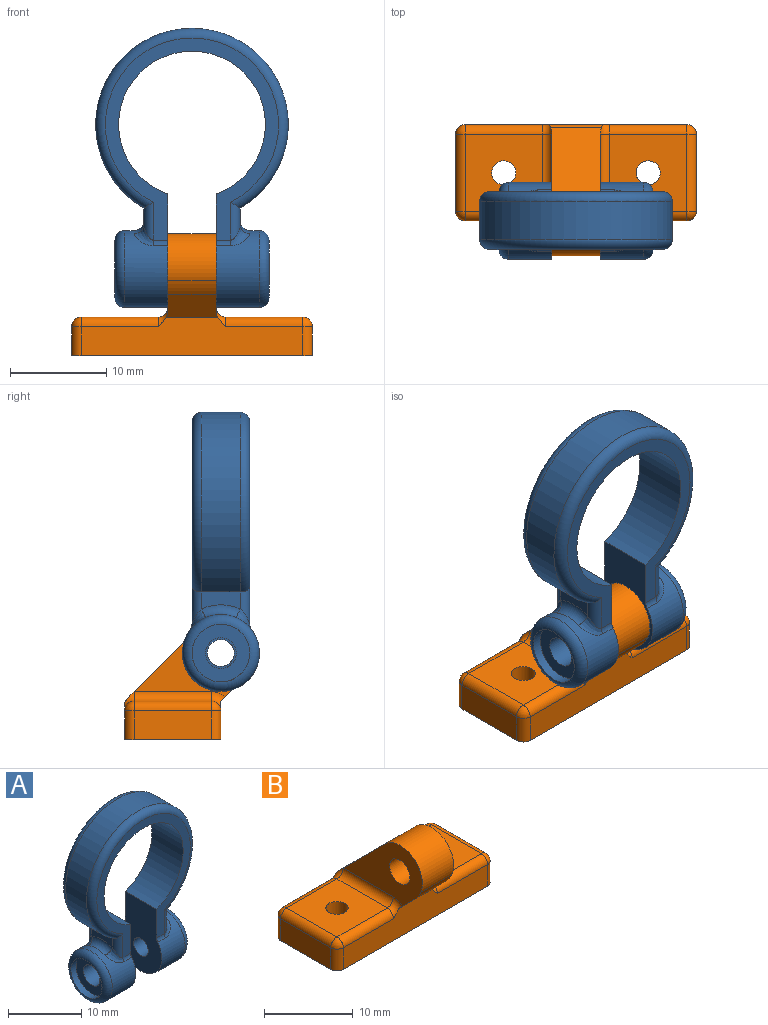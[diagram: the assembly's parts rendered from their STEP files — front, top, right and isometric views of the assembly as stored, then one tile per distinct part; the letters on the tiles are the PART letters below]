
ASSEMBLY  parts=2 mates=1
PART A: 33 faces, bbox 21.6x8.7x30.2 mm
  f0: cylinder r=1.6mm len=4.5mm, axis (1,0,0), area 45.2mm2, adj f11,f12
  f1: cylinder r=4mm len=8mm, axis (-1,0,0), area 89.1mm2, adj f10,f15,f16,f18,f19,f21,f32
  f2: cylinder r=10mm len=20mm, axis (0,1,0), area 209.4mm2, adj f6,f7,f20,f26
  f3: plane 21x18mm, normal (0,-1,0), area 75.7mm2, adj f5,f10,f11,f19,f24,f26,f28,f30
  f4: plane 21x18mm, normal (0,1,0), area 75.7mm2, adj f5,f10,f11,f15,f17,f20,f22,f23
  f5: cylinder r=7.62mm len=15.25mm, axis (0,-1,0), area 256.9mm2, adj f3,f4,f10,f11
  f6: plane 4x1.76mm, normal (-1,0,0), area 5.9mm2, adj f2,f23,f27,f28
  f7: plane 4x1.76mm, normal (1,0,0), area 5.9mm2, adj f2,f17,f18,f24
  f8: cylinder r=4mm len=8mm, axis (-1,0,0), area 89.1mm2, adj f11,f22,f25,f27,f29,f30,f31
  f9: plane 6x6mm, normal (1,0,0), area 22.1mm2, adj f14,f32
  f10: plane 11.8x8mm, normal (-1,0,0), area 69.4mm2, adj f1,f3,f4,f5,f14,f15,f19
  f11: plane 11.8x8mm, normal (1,0,0), area 67.5mm2, adj f0,f3,f4,f5,f8,f22,f30
  f12: plane 6x6mm, normal (-1,0,0), area 20.2mm2, adj f0,f13
  f13: cylinder r=3mm len=6mm, axis (-1,0,0), area 18.8mm2, adj f12,f31
  f14: cylinder r=1.4mm len=5.5mm, axis (-1,0,0), area 48.4mm2, adj f9,f10
  f15: cylinder r=1mm len=1.5mm, axis (-1,0,0), area 1mm2, adj f1,f4,f10,f16
  f16: bspline ~2.37x2.33mm, area 2.7mm2, adj f1,f15,f17,f18
  f17: cylinder r=1mm len=3.94mm, axis (0,0,1), area 4.5mm2, adj f4,f7,f16,f20
  f18: torus R=5mm, axis (1,0,0), area 5.6mm2, adj f1,f7,f16,f21
  f19: cylinder r=1mm len=1.5mm, axis (-1,0,0), area 1mm2, adj f1,f3,f10,f21
  f20: torus R=9mm, axis (0,-1,0), area 79.9mm2, adj f2,f4,f17,f23
  f21: bspline ~2.34x2.24mm, area 2.7mm2, adj f1,f18,f19,f24
  f22: cylinder r=1mm len=1.5mm, axis (-1,0,0), area 1mm2, adj f4,f8,f11,f25
  f23: cylinder r=1mm len=3.94mm, axis (0,0,-1), area 4.5mm2, adj f4,f6,f20,f25
  f24: cylinder r=1mm len=3.94mm, axis (0,0,-1), area 4.5mm2, adj f3,f7,f21,f26
  f25: bspline ~2.34x2.24mm, area 2.7mm2, adj f8,f22,f23,f27
  f26: torus R=9mm, axis (0,-1,0), area 79.9mm2, adj f2,f3,f24,f28
  f27: torus R=5mm, axis (1,0,0), area 5.6mm2, adj f6,f8,f25,f29
  f28: cylinder r=1mm len=3.94mm, axis (0,0,1), area 4.5mm2, adj f3,f6,f26,f29
  f29: bspline ~2.37x2.33mm, area 2.7mm2, adj f8,f27,f28,f30
  f30: cylinder r=1mm len=1.5mm, axis (-1,0,0), area 1mm2, adj f3,f8,f11,f29
  f31: torus R=3mm, axis (1,0,0), area 35.9mm2, adj f8,f13
  f32: torus R=3mm, axis (1,0,0), area 35.9mm2, adj f1,f9
PART B: 37 faces, bbox 25.1x15.7x12.8 mm
  f0: plane 8x8mm, normal (0,0,1), area 59.1mm2, adj f12,f23,f26,f27,f31
  f1: plane 23.11x4.11mm, normal (0,-1,0), area 75.1mm2, adj f6,f9,f16,f17,f26,f29,f32,f33
  f2: plane 8x3mm, normal (1,0,0), area 24mm2, adj f6,f24,f27,f29
  f3: plane 23.03x3.61mm, normal (0,1,0), area 72.8mm2, adj f6,f20,f22,f23,f24,f30,f35,f36
  f4: plane 8x3mm, normal (-1,0,0), area 24mm2, adj f6,f17,f19,f20
  f5: plane 8x8mm, normal (0,0,1), area 59.1mm2, adj f11,f16,f19,f22,f34
  f6: plane 25x10mm, normal (0,0,-1), area 239.3mm2, adj f1,f2,f3,f4,f11,f12,f17,f20
  f7: plane 7.36x7.36mm, normal (0,0.71,0.71), area 52.1mm2, adj f8,f10,f15,f30,f35,f36
  f8: plane 12.63x8.26mm, normal (-1,0,0), area 53.2mm2, adj f7,f9,f13,f14,f15,f33,f34
  f9: plane 5.38x2.39mm, normal (0,-0.71,-0.71), area 17mm2, adj f1,f8,f10,f14,f32,f33
  f10: plane 12.63x8.26mm, normal (1,0,0), area 53.2mm2, adj f7,f9,f13,f14,f15,f31,f32
  f11: cylinder r=1.25mm len=4mm, axis (0,0,1), area 31.4mm2, adj f5,f6
  f12: cylinder r=1.25mm len=4mm, axis (0,0,1), area 31.4mm2, adj f0,f6
  f13: cylinder r=1.6mm len=5mm, axis (-1,0,0), area 50.3mm2, adj f8,f10
  f14: cylinder r=4.5mm len=5mm, axis (-1,0,0), area 8.5mm2, adj f8,f9,f10,f15
  f15: cylinder r=3.5mm len=5.98mm, axis (-1,0,0), area 48.3mm2, adj f7,f8,f10,f14
  f16: cylinder r=1mm len=8mm, axis (-1,0,0), area 12.6mm2, adj f1,f5,f18,f33
  f17: cylinder r=1mm len=3mm, axis (0,0,1), area 4.7mm2, adj f1,f4,f6,f18
  f18: sphere r=1mm, area 1.6mm2, adj f16,f17,f19
  f19: cylinder r=1mm len=8mm, axis (0,1,0), area 12.6mm2, adj f4,f5,f18,f21
  f20: cylinder r=1mm len=3mm, axis (0,0,-1), area 4.7mm2, adj f3,f4,f6,f21
  f21: sphere r=1mm, area 1.6mm2, adj f19,f20,f22
  f22: cylinder r=1mm len=8mm, axis (1,0,0), area 12.6mm2, adj f3,f5,f21,f35
  f23: cylinder r=1mm len=8mm, axis (1,0,0), area 12.6mm2, adj f0,f3,f25,f30
  f24: cylinder r=1mm len=3mm, axis (0,0,1), area 4.7mm2, adj f2,f3,f6,f25
  f25: sphere r=1mm, area 1.6mm2, adj f23,f24,f27
  f26: cylinder r=1mm len=8mm, axis (-1,0,0), area 12.6mm2, adj f0,f1,f28,f32
  f27: cylinder r=1mm len=8mm, axis (0,-1,0), area 12.6mm2, adj f0,f2,f25,f28
  f28: sphere r=1mm, area 1.6mm2, adj f26,f27,f29
  f29: cylinder r=1mm len=3mm, axis (0,0,-1), area 4.7mm2, adj f1,f2,f6,f28
  f30: torus R=2mm, axis (-1,0,0), area 1.4mm2, adj f3,f7,f23,f31,f36
  f31: cylinder r=1mm len=8mm, axis (0,1,0), area 12.6mm2, adj f0,f10,f30,f32
  f32: torus R=2mm, axis (-1,0,0), area 2.1mm2, adj f1,f9,f10,f26,f31
  f33: torus R=2mm, axis (-1,0,0), area 2.1mm2, adj f1,f8,f9,f16,f34
  f34: cylinder r=1mm len=8mm, axis (0,1,0), area 12.6mm2, adj f5,f8,f33,f35
  f35: torus R=2mm, axis (-1,0,0), area 1.4mm2, adj f3,f7,f22,f34,f36
  f36: cylinder r=1mm len=5.92mm, axis (1,0,0), area 4.4mm2, adj f3,f7,f30,f35
PLACE A t=(15.29,-0.35,5.69)mm
PLACE B t=(15.29,2.65,-18.31)mm
MATE revolute A.f0 <-> B.f13  axis (1,0,0) through (12.79,-2.35,-9.31)mm
